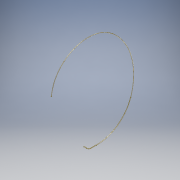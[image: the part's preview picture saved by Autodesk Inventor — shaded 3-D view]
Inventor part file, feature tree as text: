
AUTODESK INVENTOR PART (.ipt)
format: ipt  version: 2018 (Build 220112000, 112)  size: 261,632 bytes
history: native  units: mm
features: sketch x8, other x4, sweep x3, projected_geometry x2, extrude x2, plane x1
ambient origin geometry x8: Origin, YZ Plane, XZ Plane, XY Plane, X Axis, Y Axis, Z Axis, Center Point
bodies: Solid1 (feature_tree)
feature tree (20):
  sweep  "Sweep1"
  plane  "Work Plane1"
  sketch  "Sketch4"  dims[d8=6.5mm d10=37.154276mm]
  sweep  "Sweep2"
  sweep  "Sweep3"
  sketch  "Sketch1"  dims[d0=61.0mm d1=14.5mm]
  sketch  "Sketch2"  dims[d2=40.0mm d3=37.0mm]
  sketch  "Sketch3"  dims[d5=14.5mm d6=14.0mm]
  other  "Srf1"
  sketch  "Sketch5"  dims[d11=59.15489mm d12=43.599014mm]
  other  "Srf2"
  sketch  "3D Sketch3"
  sketch  "Sketch6"  dims[d16=6.0mm]
  projected_geometry  "Projected Loop1"
  sketch  "Sketch7"  dims[d18=23.09182mm d20=49.575294mm d21=31.193891mm d22=1.578841mm d23=0.5mm d24=0.0mm d25=0.0mm d26=3.0mm d27=0.0mm d28=0.5mm d29=2.5mm d30=1.0mm d31=4.0mm d32=5.0mm d33=0.0mm d34=0.0mm d35=0.0mm d36=0.0mm d37=0.0mm d38=0.0mm d39=36.0mm d40=7.5mm d41=30.0mm d42=6.0mm]
  projected_geometry  "Projected Loop2"
  extrude  "ExtrusionSrf1"  Depth=37.154276mm
  extrude  "ExtrusionSrf2"  Depth=43.599014mm
  other  "3D Intersection1"
  other  "3D Intersection2"
